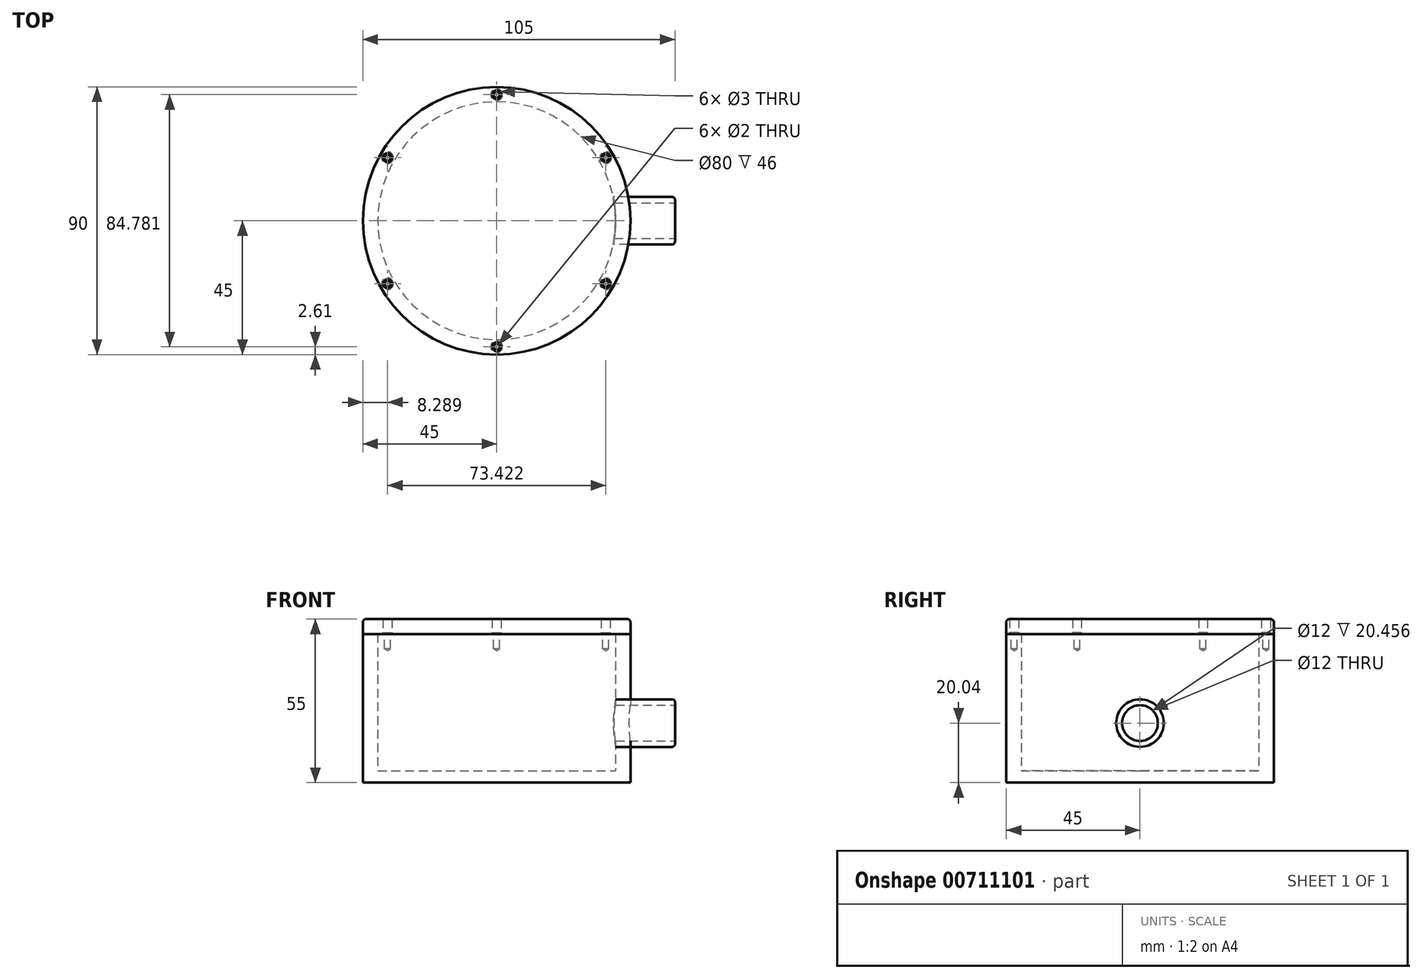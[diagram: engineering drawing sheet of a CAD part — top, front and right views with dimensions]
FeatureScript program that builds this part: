
annotation { "Feature Type Name" : "Feature", "Feature Type Description" : "" }
export const myFeature = defineFeature(function(context is Context, id is Id, definition is map)
    precondition{}
    {
        {
            var Q0;
            Q0=qCreatedBy(makeId("Front.planeOp"),FACE);
            var sketch = newSketch(context, id + "F0", { "sketchPlane" : qUnion([Q0])});
            skLineSegment(sketch, "E0", {"start": v(0, 0) * mm, "end": v(45, 0) * mm});
            skLineSegment(sketch, "E1", {"start": v(45, 0) * mm, "end": v(45, 50) * mm});
            skLineSegment(sketch, "E2", {"start": v(45, 50) * mm, "end": v(40, 50) * mm});
            skLineSegment(sketch, "E3", {"start": v(40, 50) * mm, "end": v(40, 4) * mm});
            skLineSegment(sketch, "E4", {"start": v(40, 4) * mm, "end": v(0, 4) * mm});
            skLineSegment(sketch, "E5", {"start": v(0, 4) * mm, "end": v(0, 0) * mm});
            skLineSegment(sketch, "E6", {"start": v(0, 0) * mm, "end": v(0, 64.7) * mm, "construction": true});
            skPoint(sketch, "E6.endSnap0", {"position": v(0, 2) * mm});
            skPoint(sketch, "E7", {"position": v(45, 25) * mm});
            skLineSegment(sketch, "E8", {"start": v(45, 25) * mm, "end": v(40, 25) * mm, "construction": true});
            skSolve(sketch);
        }
        {
            var Q0;
            Q0=makeQuery(id+"F0.imprint","IMPRINT",FACE,{"disambiguationData":[TD([[makeQuery(id+"F0.imprint","IMPRINT",EDGE,{"derivedFrom":sQuery(id+"F0.wireOp",EDGE,"E0")}),1.0]])]});
            var Q1;
            Q1=sQuery(id+"F0.wireOp",EDGE,"E6");
            revolve(context, id + "F1", {"surfaceOperationType" : NewSurfaceOperationType.NEW, "entities" : qUnion([Q0]), "axis" : qUnion([Q1]), "revolveType" : RevolveType.FULL});
        }
        {
            var Q0;
            Q0=qCreatedBy(makeId("Right.planeOp"),FACE);
            cPlane(context, id + "F2", {"entities" : qUnion([Q0]), "cplaneType" : CPlaneType.OFFSET, "offset" : 45 * mm, "width" : 150 * mm, "height" : 150 * mm});
        }
        {
            var Q0;
            Q0=qCreatedBy(id+"F2.planeOp",FACE);
            var sketch = newSketch(context, id + "F3", { "sketchPlane" : qUnion([Q0])});
            skCircle(sketch, "E9", {"center": v(0, 20.04) * mm, "radius": 8 * mm});
            skSolve(sketch);
        }
        {
            var Q0;
            Q0=makeQuery(id+"F3.imprint","IMPRINT",FACE,{"disambiguationData":[TD([[makeQuery(id+"F3.imprint","IMPRINT",EDGE,{"derivedFrom":sQuery(id+"F3.wireOp",EDGE,"E9")}),1.0]])]});
            var Q1;
            Q1=makeQuery(id+"F1.opRevolve","SWEPT_FACE",FACE,{"disambiguationData":[OSD([sQuery(id+"F0.wireOp",EDGE,"E3")])]});
            extrude(context, id + "F4", {"entities" : qUnion([Q0]), "depth" : 15 * mm, "offsetDistance" : 25 * mm, "hasSecondDirection" : true, "secondDirectionBound" : SecondDirectionBoundingType.UP_TO_SURFACE, "secondDirectionOppositeDirection" : true, "secondDirectionDepth" : 15 * mm, "secondDirectionBoundEntityFace" : qUnion([Q1])});
        }
        {
            var Q0;
            {var subQ0=sQuery(id+"F3.wireOp",EDGE,"E9");Q0=makeQuery(id+"F4.opExtrude","CAP_FACE",FACE,{"disambiguationData":[OSD([subQ0]),topologyDisambiguationEdgeConnected([makeQuery(id+"F3.imprint","IMPRINT",EDGE,{"derivedFrom":subQ0})])],"isStart":false});}
            var sketch = newSketch(context, id + "F5", { "sketchPlane" : qUnion([Q0])});
            skCircle(sketch, "E10", {"center": v(0, 20.04) * mm, "radius": 6 * mm});
            skSolve(sketch);
        }
        {
            var Q0;
            {var subQ0=sQuery(id+"F3.wireOp",EDGE,"E9");Q0=makeQuery(id+"F4.opExtrude","CAP_EDGE",EDGE,{"disambiguationData":[OSD([subQ0]),topologyDisambiguationEdgeConnected([makeQuery(id+"F3.imprint","IMPRINT",EDGE,{"derivedFrom":subQ0})])],"isStart":false});}
            var Q1;
            Q1=makeQuery(id+"F4.boolean.opBoolean","INTERSECT",EDGE,{"derivedFrom":[makeQuery(id+"F1.opRevolve","SWEPT_FACE",FACE,{"disambiguationData":[OSD([sQuery(id+"F0.wireOp",EDGE,"E1")])]}),makeQuery(id+"F4.opExtrude","SWEPT_FACE",FACE,{"disambiguationData":[OSD([sQuery(id+"F3.wireOp",EDGE,"E9")])]})]});
            fillet(context, id + "F6", {"entities" : qUnion([Q0, Q1]), "radius" : 1 * mm, "tangentPropagation" : true, "allowEdgeOverflow" : false});
        }
        {
            var Q0;
            Q0=makeQuery(id+"F5.imprint","IMPRINT",FACE,{"disambiguationData":[TD([[makeQuery(id+"F5.imprint","IMPRINT",EDGE,{"derivedFrom":sQuery(id+"F5.wireOp",EDGE,"E10")}),1.0]])]});
            var Q1;
            Q1=sQuery(id+"F5.wireOp",EDGE,"E10");
            var Q2;
            Q2=makeQuery(id+"F1.opRevolve","SWEPT_FACE",FACE,{"disambiguationData":[OSD([sQuery(id+"F0.wireOp",EDGE,"E3")])]});
            extrude(context, id + "F7", {"entities" : qUnion([Q0]), "operationType" : NewBodyOperationType.REMOVE, "surfaceEntities" : qUnion([Q1]), "oppositeDirection" : true, "depth" : 25 * mm, "endBoundEntityFace" : qUnion([Q2]), "offsetDistance" : 25 * mm});
        }
        {
            var Q0;
            Q0=makeQuery(id+"F1.opRevolve","SWEPT_FACE",FACE,{"disambiguationData":[OSD([sQuery(id+"F0.wireOp",EDGE,"E2")])]});
            cPlane(context, id + "F8", {"entities" : qUnion([Q0]), "cplaneType" : CPlaneType.OFFSET, "offset" : 0 * mm, "width" : 150 * mm, "height" : 150 * mm});
        }
        {
            var Q0;
            Q0=qCreatedBy(id+"F8.planeOp",FACE);
            var sketch = newSketch(context, id + "F9", { "sketchPlane" : qUnion([Q0])});
            skCircle(sketch, "E11", {"center": v(0, 0) * mm, "radius": 45 * mm});
            skPoint(sketch, "E12", {"position": v(0, 42.4) * mm});
            skPoint(sketch, "E13.1.0", {"position": v(-36.71, 21.2) * mm});
            skPoint(sketch, "E13.2.0", {"position": v(-36.71, -21.2) * mm});
            skPoint(sketch, "E14.0.3.0", {"position": v(0, -42.4) * mm});
            skPoint(sketch, "E14.0.4.0", {"position": v(36.71, -21.2) * mm});
            skPoint(sketch, "E14.0.5.0", {"position": v(36.71, 21.2) * mm});
            skSolve(sketch);
        }
        {
            var Q0;
            Q0=makeQuery(id+"F9.imprint","IMPRINT",FACE,{"disambiguationData":[TD([[makeQuery(id+"F9.imprint","IMPRINT",EDGE,{"derivedFrom":sQuery(id+"F9.wireOp",EDGE,"E11")}),1.0]])]});
            extrude(context, id + "F10", {"entities" : qUnion([Q0]), "depth" : 5 * mm, "offsetDistance" : 25 * mm});
        }
        {
            var Q0;
            Q0=makeQuery(id+"F10.opExtrude","CAP_EDGE",EDGE,{"disambiguationData":[OSD([sQuery(id+"F9.wireOp",EDGE,"E11")])],"isStart":false});
            fillet(context, id + "F11", {"entities" : qUnion([Q0]), "radius" : 1 * mm, "tangentPropagation" : true, "allowEdgeOverflow" : false});
        }
        {
            var Q0;
            Q0=sQuery(id+"F9.wireOp",VERTEX,"E12");
            var Q1;
            Q1=sQuery(id+"F9.wireOp",VERTEX,"E14.0.5.0");
            var Q2;
            Q2=sQuery(id+"F9.wireOp",VERTEX,"E14.0.4.0");
            var Q3;
            Q3=sQuery(id+"F9.wireOp",VERTEX,"E14.0.3.0");
            var Q4;
            Q4=sQuery(id+"F9.wireOp",VERTEX,"E13.2.0");
            var Q5;
            Q5=sQuery(id+"F9.wireOp",VERTEX,"E13.1.0");
            var Q6;
            Q6=makeQuery(id+"F1.opRevolve","SWEPT_BODY",BODY,{"disambiguationData":[OSD([sQuery(id+"F0.wireOp",EDGE,"E0"),sQuery(id+"F0.wireOp",EDGE,"E1"),sQuery(id+"F0.wireOp",EDGE,"E2"),sQuery(id+"F0.wireOp",EDGE,"E3"),sQuery(id+"F0.wireOp",EDGE,"E4"),sQuery(id+"F0.wireOp",EDGE,"E5")])]});
            hole(context, id + "F12", {"style" : HoleStyle.SIMPLE, "endStyle" : HoleEndStyle.BLIND, "holeDiameter" : 2 * mm, "majorDiameter" : 5 * mm, "holeDepth" : 5 * mm, "isTappedThrough" : true, "tappedDepth" : 12 * mm, "tapClearance" : 3, "startFromSketch" : true, "locations" : qUnion([Q0, Q1, Q2, Q3, Q4, Q5]), "scope" : qUnion([Q6])});
        }
        {
            var Q0;
            Q0=sQuery(id+"F9.wireOp",VERTEX,"E12");
            var Q1;
            Q1=sQuery(id+"F9.wireOp",VERTEX,"E14.0.5.0");
            var Q2;
            Q2=sQuery(id+"F9.wireOp",VERTEX,"E14.0.4.0");
            var Q3;
            Q3=sQuery(id+"F9.wireOp",VERTEX,"E14.0.3.0");
            var Q4;
            Q4=sQuery(id+"F9.wireOp",VERTEX,"E13.2.0");
            var Q5;
            Q5=sQuery(id+"F9.wireOp",VERTEX,"E13.1.0");
            var Q6;
            Q6=makeQuery(id+"F10.opExtrude","SWEPT_BODY",BODY,{"disambiguationData":[OSD([sQuery(id+"F9.wireOp",EDGE,"E11")])]});
            hole(context, id + "F13", {"style" : HoleStyle.C_SINK, "endStyle" : HoleEndStyle.BLIND, "oppositeDirection" : true, "holeDiameter" : 3 * mm, "cSinkDiameter" : 4 * mm, "cSinkAngle" : 90 * degree, "majorDiameter" : 5 * mm, "holeDepth" : 5 * mm, "isTappedThrough" : true, "tappedDepth" : 12 * mm, "tapClearance" : 3, "startFromSketch" : true, "locations" : qUnion([Q0, Q1, Q2, Q3, Q4, Q5]), "scope" : qUnion([Q6])});
        }
    });
